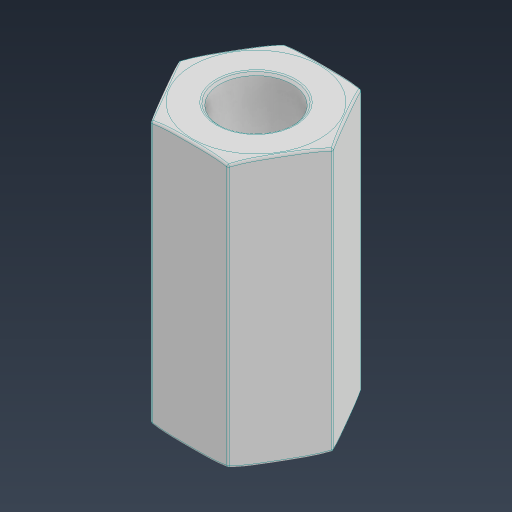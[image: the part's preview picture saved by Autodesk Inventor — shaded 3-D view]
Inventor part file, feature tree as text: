
AUTODESK INVENTOR PART (.ipt)
format: ipt  version: 2024.3 (Build 283343000, 343)  size: 200,704 bytes
history: native  units: in
note: dims shown in document units (in); Inventor stores cm internally (conversion verified against a paired STEP export)
features: fillet x1
ambient origin geometry x8: Origin, YZ Plane, XZ Plane, XY Plane, X Axis, Y Axis, Z Axis, Center Point
bodies: Solid1 (feature_tree)
feature tree (1):
  fillet  "Fillet1"  [1 undecoded]
note: 1 required parameter value undecoded (feature->parameter linkage not recoverable at this tier; creation-order binding heuristic only, values carry confidence <= 0.55)
